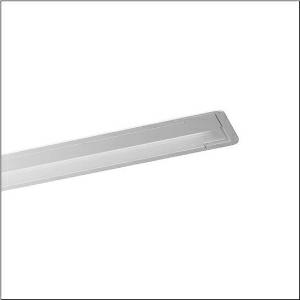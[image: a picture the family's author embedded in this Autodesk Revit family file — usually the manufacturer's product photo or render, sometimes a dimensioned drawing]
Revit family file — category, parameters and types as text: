
# Revit family: taris_r__21_5mt126d04wa_d05e
name_source: partatom
category: Lighting Fixtures
units: mm (PartAtom-declared; Revit-internal decimal feet)

## family parameters
Cut with Voids When Loaded = No
Host = Face
Light Source = No
Part Type = Normal
Room Calculation Point = No
Round Connector Dimension = Use Diameter
Shared = No

## types (1)
- --- (1 x LED, 4080 lm, 28.9 W, 4000K)
    Apparent Load = 29 VA
    CIE Flux Codes = 66 91 98 100 100
    Color Rendering = 80
    Color Temperature = 4000K
    Default Elevation = 1800 mm
    Description = Taris® 21, office luminaire, primary light control with wallwasher, primary anti-glare with micro louvre, primary optical cover: axial lens, of PMMA, structured, light emission: direct distribution, primary light characteristic: asymmetric, installation type: recessed, LED rated luminous flux: 4.080 lm, light colour: 840, colour temperature: 4000K, control gear: ECG DALI, with terminal, 5-pole, mains connection: 230V, AC, 50Hz, rated input power: 29W, luminaire housing, of plastic, pure white, module: M625, length: 1.250 mm, width: 144 mm, height: 76mm, recess depth: 106 mm, protection rating (complete): IP20, insulation class (complete): insulation class I (protective earthing), certification: CE, protection symbol: F, impact resistance: IK02, permissible ambient temperature for indoor applications: 0..+35°C, standard: EN 50419, packaging unit: 1 piece
    Height = 0 mm  [stored 0 ft]
    Lamp = 1 x LED
    Lamp Light Flux = 4080 lm
    Lamp Power = 28.9 W
    Lamp count = 1
    Length = 1243 mm
    Luminous efficacy = 141 lm/W
    Manufacturer = Siteco
    ModVariant = No
    Model = 5MT126D04WA
    Mounting Place = Ceiling
    Mounting Type = Recessed
    Number of Poles = 1
    OnlyDefault = Yes
    Power Factor = 1
    Product Name = Taris® 21
    Product group = office luminaire | ceiling recessed
    ProductGroupID = 400
    Protection Class = Protection class I
    Protection Degree = IP 20
    RLX_Detail_Level = 1
    RlxData = <blob elided: 29625 chars, md5=aa27b3fc>
    Socket = socket
    Standby Power = 0 W
    System Light Flux = 4080 lm
    System Power = 29 W
    Type Comments = factory setting: luminous flux: 100 % | dim-lin: 254 | 200 mA
    Type Image = l_1004721.jpg
    URL = http://relux.com
    VarID = @adj_130065
    Voltage = 0 V
    Weight = 0.00 kg
    Width = 144 mm

note: [stored X ft] marks values corroborated as IEEE doubles in the binary element streams (Revit-internal decimal feet)

## geometry (parser evidence)
native form markers: Blend x4, Sweep x11
no freeform markers — native parametric forms only
